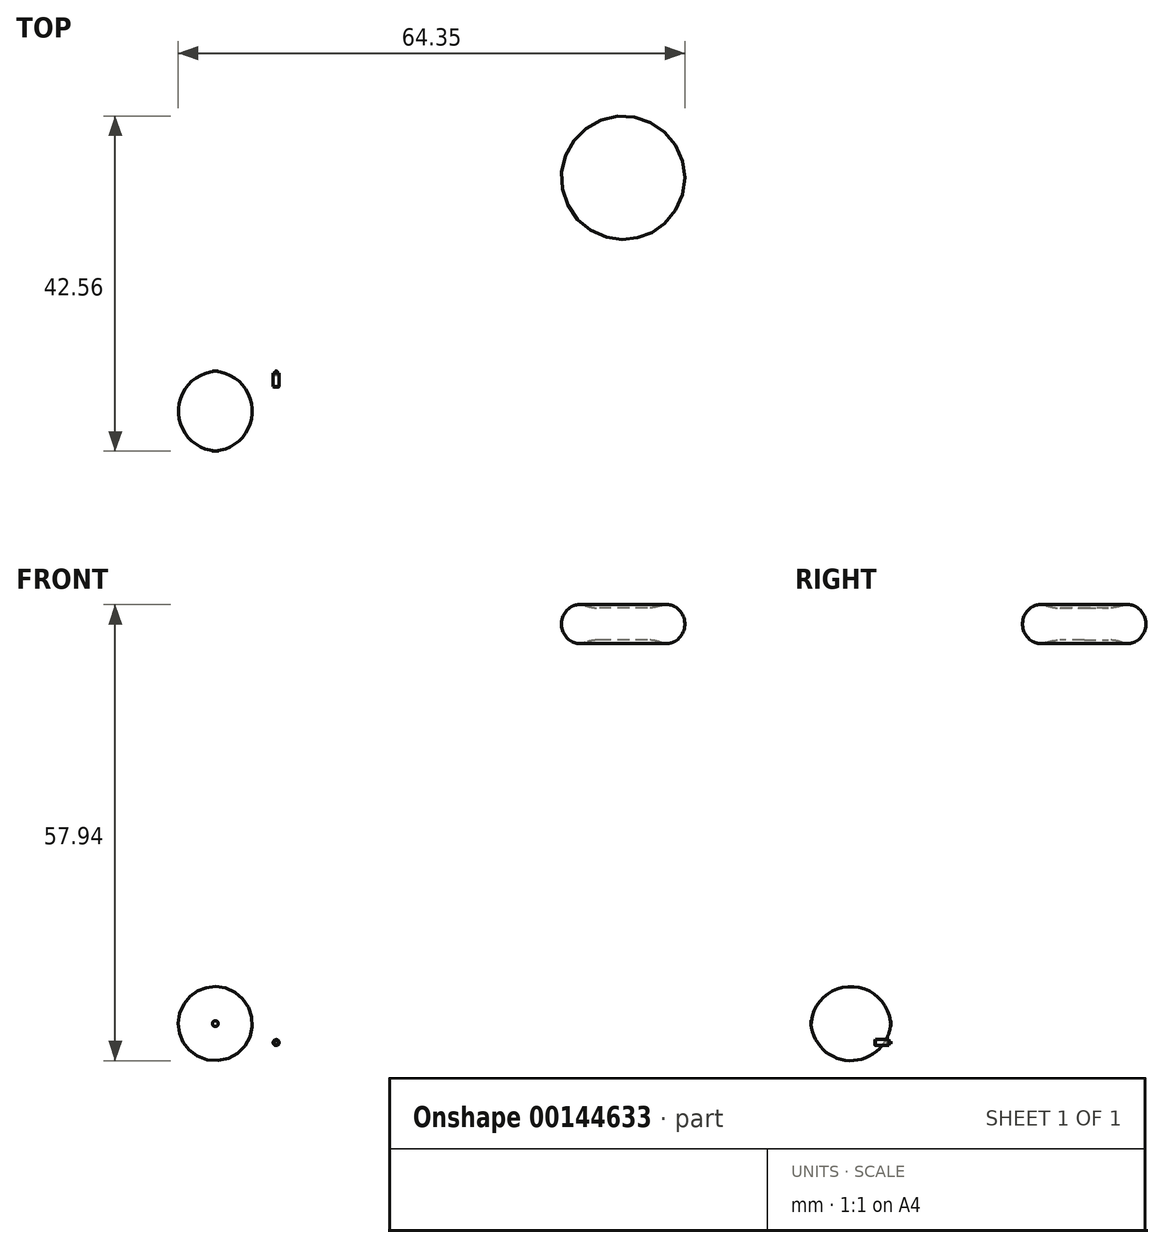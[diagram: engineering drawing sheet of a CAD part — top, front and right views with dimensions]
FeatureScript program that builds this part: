
annotation { "Feature Type Name" : "Feature", "Feature Type Description" : "" }
export const myFeature = defineFeature(function(context is Context, id is Id, definition is map)
    precondition{}
    {
        {
            var Q0;
            Q0=qCreatedBy(makeId("Top.planeOp"),FACE);
            var sketch = newSketch(context, id + "F0", { "sketchPlane" : qUnion([Q0])});
            skCircle(sketch, "E0", {"center": v(-32.8, 24.56) * mm, "radius": 7.84 * mm});
            skSolve(sketch);
        }
        {
            var Q0;
            Q0=makeQuery(id+"F0.imprint","IMPRINT",FACE,{"disambiguationData":[TD([[makeQuery(id+"F0.imprint","IMPRINT",EDGE,{"derivedFrom":sQuery(id+"F0.wireOp",EDGE,"E0")}),1.0]])]});
            extrude(context, id + "F1", {"entities" : qUnion([Q0]), "depth" : 5.08 * mm});
        }
        {
            var Q0;
            Q0=makeQuery(id+"F1.opExtrude","CAP_EDGE",EDGE,{"disambiguationData":[OSD([sQuery(id+"F0.wireOp",EDGE,"E0")])],"isStart":false});
            var Q1;
            Q1=makeQuery(id+"F1.opExtrude","CAP_EDGE",EDGE,{"disambiguationData":[OSD([sQuery(id+"F0.wireOp",EDGE,"E0")])],"isStart":true});
            fillet(context, id + "F2", {"entities" : qUnion([Q0, Q1]), "radius" : 2.54 * mm, "tangentPropagation" : true, "allowEdgeOverflow" : false});
        }
        {
            var Q0;
            Q0=makeQuery(id+"F1.opExtrude","CAP_FACE",FACE,{"disambiguationData":[OSD([sQuery(id+"F0.wireOp",EDGE,"E0")])],"isStart":true});
            extrude(context, id + "F3", {"entities" : qUnion([Q0]), "operationType" : NewBodyOperationType.ADD, "oppositeDirection" : true, "depth" : 1.02 * mm});
        }
        {
            var Q0;
            Q0=makeQuery(id+"F1.opExtrude","CAP_FACE",FACE,{"disambiguationData":[OSD([sQuery(id+"F0.wireOp",EDGE,"E0")])],"isStart":true});
            extrude(context, id + "F4", {"entities" : qUnion([Q0]), "operationType" : NewBodyOperationType.REMOVE, "oppositeDirection" : true, "depth" : 0.5 * mm});
        }
        {
            var Q0;
            Q0=makeQuery(id+"F1.opExtrude","CAP_FACE",FACE,{"disambiguationData":[OSD([sQuery(id+"F0.wireOp",EDGE,"E0")])],"isStart":false});
            extrude(context, id + "F5", {"entities" : qUnion([Q0]), "operationType" : NewBodyOperationType.REMOVE, "oppositeDirection" : true, "depth" : 0.5 * mm});
        }
        {
            var Q0;
            Q0=makeQuery(id+"F5.boolean.opBoolean","COPY",EDGE,{"derivedFrom":makeQuery(id+"F5.opExtrude","CAP_EDGE",EDGE,{"disambiguationData":[OSD([sQuery(id+"F0.wireOp",EDGE,"E0")])],"isStart":false})});
            fillet(context, id + "F6", {"entities" : qUnion([Q0]), "radius" : 5.08 * mm, "tangentPropagation" : true, "allowEdgeOverflow" : false});
        }
        {
            var Q0;
            Q0=makeQuery(id+"F4.boolean.opBoolean","COPY",EDGE,{"derivedFrom":makeQuery(id+"F4.opExtrude","CAP_EDGE",EDGE,{"disambiguationData":[OSD([sQuery(id+"F0.wireOp",EDGE,"E0")])],"isStart":false})});
            fillet(context, id + "F7", {"entities" : qUnion([Q0]), "radius" : 5.08 * mm, "tangentPropagation" : true, "allowEdgeOverflow" : false});
        }
        {
            var Q0;
            {var subQ0=sQuery(id+"F0.wireOp",EDGE,"E0");Q0=makeQuery(id+"F6.opFillet","BLEND_EDGE",EDGE,{"blendedFrom":[makeQuery(id+"F5.boolean.opBoolean","COPY",EDGE,{"derivedFrom":makeQuery(id+"F5.opExtrude","CAP_EDGE",EDGE,{"disambiguationData":[OSD([subQ0])],"isStart":false})}),makeQuery(id+"F2.opFillet","BLEND_FACE",FACE,{"disambiguationData":[OSD([subQ0])]})],"blendedInto":[makeQuery(id+"F2.opFillet","BLEND_FACE",FACE,{"disambiguationData":[OSD([subQ0])]})]});}
            fillet(context, id + "F8", {"entities" : qUnion([Q0]), "radius" : 2.03 * mm, "tangentPropagation" : true, "allowEdgeOverflow" : false});
        }
        {
            var Q0;
            {var subQ0=sQuery(id+"F0.wireOp",EDGE,"E0");Q0=makeQuery(id+"F7.opFillet","BLEND_EDGE",EDGE,{"blendedFrom":[makeQuery(id+"F4.boolean.opBoolean","COPY",EDGE,{"derivedFrom":makeQuery(id+"F4.opExtrude","CAP_EDGE",EDGE,{"disambiguationData":[OSD([subQ0])],"isStart":false})}),makeQuery(id+"F2.opFillet","BLEND_FACE",FACE,{"disambiguationData":[OSD([subQ0])]})],"blendedInto":[makeQuery(id+"F2.opFillet","BLEND_FACE",FACE,{"disambiguationData":[OSD([subQ0])]})]});}
            fillet(context, id + "F9", {"entities" : qUnion([Q0]), "radius" : 2.03 * mm, "tangentPropagation" : true, "allowEdgeOverflow" : false});
        }
        {
            var Q0;
            Q0=qCreatedBy(makeId("Front.planeOp"),FACE);
            var sketch = newSketch(context, id + "F10", { "sketchPlane" : qUnion([Q0])});
            skCircle(sketch, "E1", {"center": v(-84.6, -48.22) * mm, "radius": 5.46 * mm});
            skSolve(sketch);
        }
        {
            var Q0;
            Q0=makeQuery(id+"F10.imprint","IMPRINT",FACE,{"disambiguationData":[TD([[makeQuery(id+"F10.imprint","IMPRINT",EDGE,{"derivedFrom":sQuery(id+"F10.wireOp",EDGE,"E1")}),1.0]])]});
            extrude(context, id + "F11", {"entities" : qUnion([Q0]), "depth" : 10.16 * mm});
        }
        {
            var Q0;
            Q0=makeQuery(id+"F11.opExtrude","CAP_EDGE",EDGE,{"disambiguationData":[OSD([sQuery(id+"F10.wireOp",EDGE,"E1")])],"isStart":false});
            fillet(context, id + "F12", {"entities" : qUnion([Q0]), "radius" : 5.08 * mm, "tangentPropagation" : true, "allowEdgeOverflow" : false});
        }
        {
            var Q0;
            Q0=makeQuery(id+"F11.opExtrude","CAP_EDGE",EDGE,{"disambiguationData":[OSD([sQuery(id+"F10.wireOp",EDGE,"E1")])],"isStart":true});
            fillet(context, id + "F13", {"entities" : qUnion([Q0]), "radius" : 5.08 * mm, "tangentPropagation" : true, "allowEdgeOverflow" : false});
        }
        {
            var Q0;
            Q0=qCreatedBy(makeId("Front.planeOp"),FACE);
            var sketch = newSketch(context, id + "F14", { "sketchPlane" : qUnion([Q0])});
            skCircle(sketch, "E2", {"center": v(-76.88, -50.63) * mm, "radius": 0.38 * mm});
            skSolve(sketch);
        }
        {
            var Q0;
            Q0=makeQuery(id+"F14.imprint","IMPRINT",FACE,{"disambiguationData":[TD([[makeQuery(id+"F14.imprint","IMPRINT",EDGE,{"derivedFrom":sQuery(id+"F14.wireOp",EDGE,"E2")}),1.0]])]});
            extrude(context, id + "F15", {"entities" : qUnion([Q0]), "depth" : 2.03 * mm});
        }
        {
            var Q0;
            Q0=makeQuery(id+"F15.opExtrude","CAP_EDGE",EDGE,{"disambiguationData":[OSD([sQuery(id+"F14.wireOp",EDGE,"E2")])],"isStart":true});
            fillet(context, id + "F16", {"entities" : qUnion([Q0]), "radius" : 0.24 * mm, "tangentPropagation" : true, "allowEdgeOverflow" : false});
        }
        {
            var Q0;
            Q0=makeQuery(id+"F15.opExtrude","CAP_EDGE",EDGE,{"disambiguationData":[OSD([sQuery(id+"F14.wireOp",EDGE,"E2")])],"isStart":false});
            chamfer(context, id + "F17", {"entities" : qUnion([Q0]), "chamferType" : ChamferType.OFFSET_ANGLE, "width" : 0.1 * mm, "oppositeDirection" : false, "angle" : 30 * degree, "tangentPropagation" : true});
        }
    });
